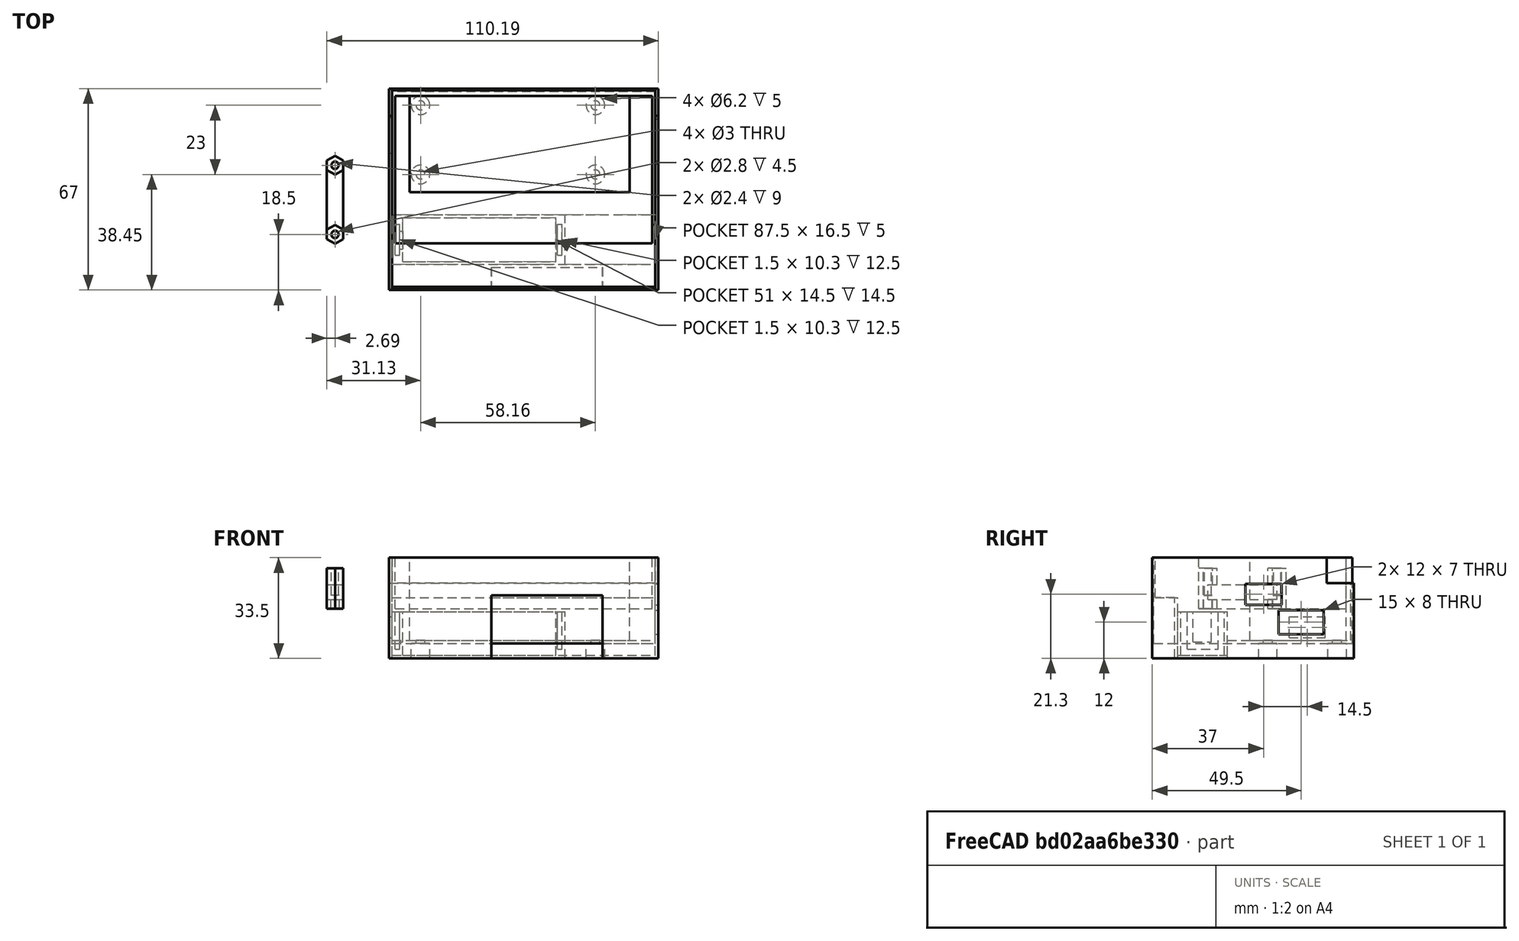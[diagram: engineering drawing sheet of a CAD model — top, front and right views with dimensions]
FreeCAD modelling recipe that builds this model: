
FCSTD DOCUMENT  (FreeCAD 0.18R16131 (Git))
Label: cyberdeck_pizero_14500
License: All rights reserved
LicenseURL: http://en.wikipedia.org/wiki/All_rights_reserved
objects: Part::Cut×25, Part::Box×19, Part::Cylinder×12, Part::Prism×2, Part::MultiFuse×1
note: 59 computed .brp shape members not serialized (recipe doc carries the construction recipe); baked Part::Feature solids carry a one-line shape summary decoded from their .brp

FEATURE [Part::Box] Box  label="Cube(screen)"
  AttacherType = Attacher::AttachEngine3D
  Height = 17
  Length = 85.5
  Placement = pos=(0,7,0) rot=(0,0,1;0rad)
  Width = 49
FEATURE [Part::Box] Box001  label="Cube(pizero)"
  AttacherType = Attacher::AttachEngine3D
  Height = 27.5
  Length = 73.2
  Placement = pos=(4.8,24,-10.5) rot=(0,0,1;0rad)
  Width = 32
FEATURE [Part::Box] Box003  label="Cube(outer_thinner)"
  AttacherType = Attacher::AttachEngine3D
  Height = 28.5
  Length = 87.5
  Placement = pos=(-1,-8,-11.5) rot=(0,0,1;0rad)
  Width = 66
FEATURE [Part::Cylinder] Cylinder  label="Cylinder(right_shaft_bottom"
  Angle = 360
  AttacherType = Attacher::AttachEngine3D
  Height = 10
  Placement = pos=(66.6,52.95,-17) rot=(0,0,1;0rad)
  Radius = 1.5
FEATURE [Part::Cylinder] Cylinder001  label="Cylinder001(left_shaft_bottom)"
  Angle = 360
  AttacherType = Attacher::AttachEngine3D
  Height = 10
  Placement = pos=(8.44,52.95,-17) rot=(0,0,1;0rad)
  Radius = 1.5
FEATURE [Part::Box] Box004  label="Cube(screen_cutout)"
  AttacherType = Attacher::AttachEngine3D
  Height = 27.5
  Length = 87.5
  Placement = pos=(-1,0,-10.5) rot=(0,0,1;0rad)
  Width = 57.5
FEATURE [Part::Box] Box005  label="Cube(screen_to_pcb_cutout)"
  AttacherType = Attacher::AttachEngine3D
  Height = 21
  Length = 37
  Placement = pos=(32,-8.5,-16.5) rot=(0,0,1;0rad)
  Width = 7.5
FEATURE [Part::Box] Box002  label="Cube(screen_to_pcb)"
  AttacherType = Attacher::AttachEngine3D
  Height = 13.3
  Length = 87.5
  Placement = pos=(-1,-7.5,3.7) rot=(0,0,1;0rad)
  Width = 7.5
FEATURE [Part::Box] Box006  label="Cube(usb_port)"
  AttacherType = Attacher::AttachEngine3D
  Height = 8
  Length = 10
  Placement = pos=(77.5,33.5,-8.5) rot=(0,0,1;0rad)
  Width = 15
FEATURE [Part::Box] Box014  label="Cube(outer_14500)"
  AttacherType = Attacher::AttachEngine3D
  Height = 33.5
  Length = 89.5
  Placement = pos=(-2,-8.5,-16.5) rot=(0,0,1;0rad)
  Width = 67
FEATURE [Part::Box] Box021  label="Cube(screen_cutout_14500)"
  AttacherType = Attacher::AttachEngine3D
  Height = 32.5
  Length = 87.5
  Placement = pos=(-1,0,-15.5) rot=(0,0,1;0rad)
  Width = 16.5
FEATURE [Part::Box] Box022  label="Cube"
  AttacherType = Attacher::AttachEngine3D
  Height = 14.5
  Length = 51
  Placement = pos=(1,1,0) rot=(0,0,1;0rad)
  Width = 14.5
FEATURE [Part::Box] Box023  label="Cube001"
  AttacherType = Attacher::AttachEngine3D
  Height = 15.5
  Length = 57.5
  Placement = pos=(-2.5,0,-1) rot=(0,0,1;0rad)
  Width = 16.5
FEATURE [Part::Box] Box024  label="Cube002(minus_spring)"
  AttacherType = Attacher::AttachEngine3D
  Height = 12.5
  Length = 1.5
  Placement = pos=(-1.5,3.1,2) rot=(0,0,1;0rad)
  Width = 10.3
FEATURE [Part::Box] Box025  label="Cube003(plus_end)"
  AttacherType = Attacher::AttachEngine3D
  Height = 12.5
  Length = 1.5
  Placement = pos=(52.5,3.1,2) rot=(0,0,1;0rad)
  Width = 10.3
FEATURE [Part::Box] Box026  label="Cube002(minus_spring_gap)"
  AttacherType = Attacher::AttachEngine3D
  Height = 10
  Length = 5
  Placement = pos=(0,5.1,4.5) rot=(0,0,1;0rad)
  Width = 6
FEATURE [Part::Box] Box027  label="Cube003(plus_end_gap)"
  AttacherType = Attacher::AttachEngine3D
  Height = 10
  Length = 5
  Placement = pos=(47.5,5.1,4.5) rot=(0,0,1;0rad)
  Width = 6
FEATURE [Part::Cut] Cut
  Base = -> Box023
  Tool = -> Box022
FEATURE [Part::Cut] Cut001
  Base = -> Cut
  Tool = -> Box024
FEATURE [Part::Cut] Cut002
  Base = -> Cut001
  Tool = -> Box025
FEATURE [Part::Cut] Cut003
  Base = -> Cut002
  Tool = -> Box026
FEATURE [Part::Cut] Cut004
  Base = -> Cut003
  Placement = pos=(1.5,0,-15.5) rot=(0,0,1;0rad)
  Tool = -> Box027
FEATURE [Part::Box] Box028  label="Cube(micro_usb_port)"
  AttacherType = Attacher::AttachEngine3D
  Height = 7
  Length = 10
  Placement = pos=(77.5,22.5,1.3) rot=(0,0,1;0rad)
  Width = 12
FEATURE [Part::Box] Box029  label="Cube(micro_sdcard)"
  AttacherType = Attacher::AttachEngine3D
  Height = 7
  Length = 10
  Placement = pos=(-2,37,-9.7) rot=(0,0,1;0rad)
  Width = 12
FEATURE [Part::Cylinder] Cylinder002  label="Cylinder002(right_clearance_bottom)"
  Angle = 360
  AttacherType = Attacher::AttachEngine3D
  Height = 5
  Placement = pos=(66.6,52.95,-16.5) rot=(0,0,1;0rad)
  Radius = 3.1
FEATURE [Part::Cylinder] Cylinder003  label="Cylinder001(left_clearance_bottom)"
  Angle = 360
  AttacherType = Attacher::AttachEngine3D
  Height = 5
  Placement = pos=(8.44,52.95,-16.5) rot=(0,0,1;0rad)
  Radius = 3.1
FEATURE [Part::Prism] Prism  label="Prism(top)"
  AttacherType = Attacher::AttachEngine3D
  Circumradius = 3.1
  Height = 13.5
  Placement = pos=(-20,10,0) rot=(0,0,1;0.523599rad)
  Polygon = 6
FEATURE [Part::Cylinder] Cylinder004  label="Cylinder(top_m2)"
  Angle = 360
  AttacherType = Attacher::AttachEngine3D
  Height = 9
  Placement = pos=(-20,10,4.5) rot=(0,0,1;0rad)
  Radius = 1.2
FEATURE [Part::Prism] Prism001  label="Prism001(bottom)"
  AttacherType = Attacher::AttachEngine3D
  Circumradius = 3.1
  Height = 13.5
  Placement = pos=(-20,33,0) rot=(0,0,1;0.523599rad)
  Polygon = 6
FEATURE [Part::Cylinder] Cylinder005  label="Cylinder001(bottom_m2)"
  Angle = 360
  AttacherType = Attacher::AttachEngine3D
  Height = 9
  Placement = pos=(-20,33,4.5) rot=(0,0,1;0rad)
  Radius = 1.2
FEATURE [Part::Box] Box030  label="Cube002(standoff_join)"
  AttacherType = Attacher::AttachEngine3D
  Height = 5
  Length = 5.4
  Placement = pos=(-22.69,10,3) rot=(0,0,1;0rad)
  Width = 23
FEATURE [Part::MultiFuse] Fusion
  Shapes = -> [Box030,Prism001,Prism]
FEATURE [Part::Cylinder] Cylinder006  label="Cylinder001(left_shaft_top)"
  Angle = 360
  AttacherType = Attacher::AttachEngine3D
  Height = 10
  Placement = pos=(8.44,29.95,-17) rot=(0,0,1;0rad)
  Radius = 1.5
FEATURE [Part::Cylinder] Cylinder007  label="Cylinder001(left_clearance_top)"
  Angle = 360
  AttacherType = Attacher::AttachEngine3D
  Height = 5
  Placement = pos=(8.44,29.95,-16.5) rot=(0,0,1;0rad)
  Radius = 3.1
FEATURE [Part::Cylinder] Cylinder008  label="Cylinder002(right_clearance_top)"
  Angle = 360
  AttacherType = Attacher::AttachEngine3D
  Height = 5
  Placement = pos=(66.6,29.95,-16.5) rot=(0,0,1;0rad)
  Radius = 3.1
FEATURE [Part::Cylinder] Cylinder009  label="Cylinder(right_shaft_top)"
  Angle = 360
  AttacherType = Attacher::AttachEngine3D
  Height = 10
  Placement = pos=(66.6,29.95,-17) rot=(0,0,1;0rad)
  Radius = 1.5
FEATURE [Part::Box] Box031  label="Cube002(GPIO_cutout)"
  AttacherType = Attacher::AttachEngine3D
  Height = 8.5
  Length = 89.5
  Placement = pos=(-2,49.5,8.5) rot=(0,0,1;0rad)
  Width = 9
FEATURE [Part::Cut] Cut007
  Base = -> Box014
  Tool = -> Box031
FEATURE [Part::Cut] Cut008
  Base = -> Cut007
  Tool = -> Cylinder009
FEATURE [Part::Cut] Cut009
  Base = -> Cut008
  Tool = -> Cylinder008
FEATURE [Part::Cut] Cut010
  Base = -> Cut009
  Tool = -> Cylinder007
FEATURE [Part::Cut] Cut011
  Base = -> Cut010
  Tool = -> Cylinder006
FEATURE [Part::Cut] Cut012
  Base = -> Cut011
  Tool = -> Box021
FEATURE [Part::Cut] Cut013
  Base = -> Cut012
  Tool = -> Box004
FEATURE [Part::Cut] Cut014
  Base = -> Cut013
  Tool = -> Box005
FEATURE [Part::Cut] Cut015
  Base = -> Cut014
  Tool = -> Box002
FEATURE [Part::Cut] Cut016
  Base = -> Cut015
  Tool = -> Cylinder002
FEATURE [Part::Cut] Cut017
  Base = -> Cut016
  Tool = -> Cylinder
FEATURE [Part::Cut] Cut018
  Base = -> Cut017
  Tool = -> Cylinder001
FEATURE [Part::Cut] Cut019
  Base = -> Cut018
  Tool = -> Cylinder003
FEATURE [Part::Cut] Cut020
  Base = -> Cut019
  Tool = -> Box006
FEATURE [Part::Cut] Cut021
  Base = -> Cut020
  Tool = -> Box029
FEATURE [Part::Cut] Cut022
  Base = -> Cut021
  Tool = -> Box028
FEATURE [Part::Cylinder] Cylinder010  label="Cylinder(top_m3)"
  Angle = 360
  AttacherType = Attacher::AttachEngine3D
  Height = 4.5
  Placement = pos=(-20,10,0) rot=(0,0,1;0rad)
  Radius = 1.4
FEATURE [Part::Cylinder] Cylinder011  label="Cylinder001(bottom_m3)"
  Angle = 360
  AttacherType = Attacher::AttachEngine3D
  Height = 4.5
  Placement = pos=(-20,33,0) rot=(0,0,1;0rad)
  Radius = 1.4
FEATURE [Part::Cut] Cut023
  Base = -> Fusion
  Tool = -> Cylinder004
FEATURE [Part::Cut] Cut024
  Base = -> Cut023
  Tool = -> Cylinder011
FEATURE [Part::Cut] Cut025
  Base = -> Cut024
  Tool = -> Cylinder010
FEATURE [Part::Cut] Cut026
  Base = -> Cut025
  Tool = -> Cylinder005
